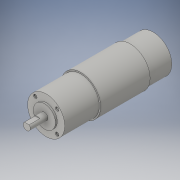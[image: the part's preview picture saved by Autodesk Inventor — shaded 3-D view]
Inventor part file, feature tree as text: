
AUTODESK INVENTOR PART (.ipt)
format: ipt  version: 2016 (Build 200138000, 138)  size: 155,648 bytes
history: native  units: in
note: dims shown in document units (in); Inventor stores cm internally (conversion verified against a paired STEP export)
features: sketch x9, extrude x7, hole x1
ambient origin geometry x8: Origin, YZ Plane, XZ Plane, XY Plane, X Axis, Y Axis, Z Axis, Center Point
bodies: Solid1 (feature_tree)
feature tree (17):
  extrude  "Extrusion1"  Depth=2.5984in TaperAngle=0.0deg
  extrude  "Extrusion2"  Depth=1.5433in TaperAngle=0.0deg
  sketch  "3D Sketch1"
  extrude  "Extrusion3"  Depth=0.0787in TaperAngle=0.0deg
  extrude  "Extrusion4"  Depth=0.7874in TaperAngle=0.0deg
  extrude  "Extrusion5"  Depth=0.4724in TaperAngle=0.0deg
  hole  "Hole1"  [1 undecoded]
  extrude  "Extrusion6"  Depth=0.6339in
  extrude  "Extrusion7"  Depth=0.3937in TaperAngle=0.0deg
  sketch  "Sketch1"  dims[d0=1.7717in d1=2.5984in d2=0.0in]
  sketch  "Sketch2"  dims[d3=1.6535in d4=1.5433in d5=0.0in]
  sketch  "Sketch3"  dims[d6=0.9843in d7=0.0787in d8=0.0in]
  sketch  "Sketch4"  dims[d9=0.315in d10=0.7874in d11=0.0in]
  sketch  "Sketch5"  dims[d12=0.1181in d13=0.4724in d14=0.0in]
  sketch  "Sketch6"  dims[d15=0.689in d16=0.4872in]
  sketch  "Sketch7"  dims[d17=1.5748in d19=360.0deg]
  sketch  "Sketch8"  dims[d21=0.128in d22=0.75in d23=0.1575in d24=0.0394in d25=0.5635in d26=0.2362in d27=0.8108in d28=1.6535in d29=0.3937in d30=0.0in d31=0.6339in d32=0.0in]
note: 1 required parameter value undecoded (feature->parameter linkage not recoverable at this tier; creation-order binding heuristic only, values carry confidence <= 0.55)
